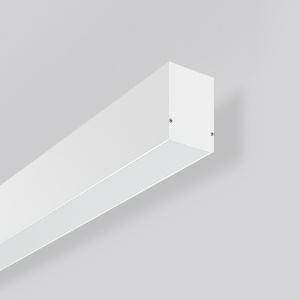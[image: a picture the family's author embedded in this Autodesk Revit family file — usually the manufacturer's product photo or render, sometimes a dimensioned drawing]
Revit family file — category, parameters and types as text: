
# Revit family: less_is_more_50_312608_002_0191
name_source: partatom
category: Lighting Fixtures
units: mm (PartAtom-declared; Revit-internal decimal feet)

## family parameters
Cut with Voids When Loaded = No
Host = Face
Light Source = No
Part Type = Normal
Room Calculation Point = No
Round Connector Dimension = Use Diameter
Shared = No

## types (1)
- LESS IS MORE 50 (1 x LED Modul 830, 2600 lm, 3000)
    Apparent Load = 20 VA
    CIE Flux Codes = 48 80 96 50 100
    Color Rendering = 80
    Color Temperature = 3000
    Default Elevation = 1800 mm
    Description = Series: LESS IS MORE 50
Linear wall luminaires. Housing: extruded aluminium profile, powder-coated. End cap aluminium powder-coated. Diffuser made of non-yellowing plastic (PMMA), opal. Direct 50%, indirect 50% light emission. Suitable for Wall (surface). LED unit with integrated converter interchangeable and removable. Suitable for through-wiring. With sensors or as a safety luminaire on request. 
Colour: traffic white, matt (RAL 9016)
Length: 1127 mm
Width: 67 mm
Height: 75 mm
Lamp: LED
Socket: without socket
Colour temperature: 3000K
Colour rendering index (CRI): 80
Light source: LED
Socket lamp2: Without base
Colour temperature: 3000K
Colour rendering index (CRI) 2: 80
System power: 20 W
Rated luminous flux: 2600 lm
Luminous efficiency: 130 lm/W
Control gear: Regulated power supply
Control gear: Regulated power supply
Protection class: I
Type of protection: IP 20
    Height = 75 mm
    Lamp = 1 x LED Modul 830
    Lamp Light Flux = 2600 lm
    Lamp count = 1
    Length = 1127 mm
    Lifetime = 50000 h
    Luminous efficacy = 130 lm/W
    Manufacturer = RZB
    ModVariant = No
    Model = 312608.002
    Mounting Place = Wall
    Mounting Type = Surface mounted
    Number of Poles = 1
    OnlyDefault = Yes
    Power Factor = 1
    Product Name = LESS IS MORE 50
    Product group = Surface mounted LED linear luminaires
    ProductGroupID = 2007
    Protection Class = Protection class I
    Protection Degree = IP 20
    RLX_Detail_Level = 1
    RLX_Emergency_Light_Flux = 0 lm
    RLX_Emergency_Type = 0
    RLX_Emergency_Type_DB = No
    RlxData = <blob elided: 39589 chars, md5=ac3c000d>
    Socket = socket
    Standby Power = 0 W
    System Light Flux = 2600 lm
    System Power = 20 W
    Type Comments = Product without accessories
    Type Image = 312606.002.jpg
    URL = http://relux.com
    VarID = ---
    Voltage = 0 V
    Weight = 0.00 kg
    Width = 67 mm

## geometry (parser evidence)
native form markers: Blend x4, Sweep x13
no freeform markers — native parametric forms only
